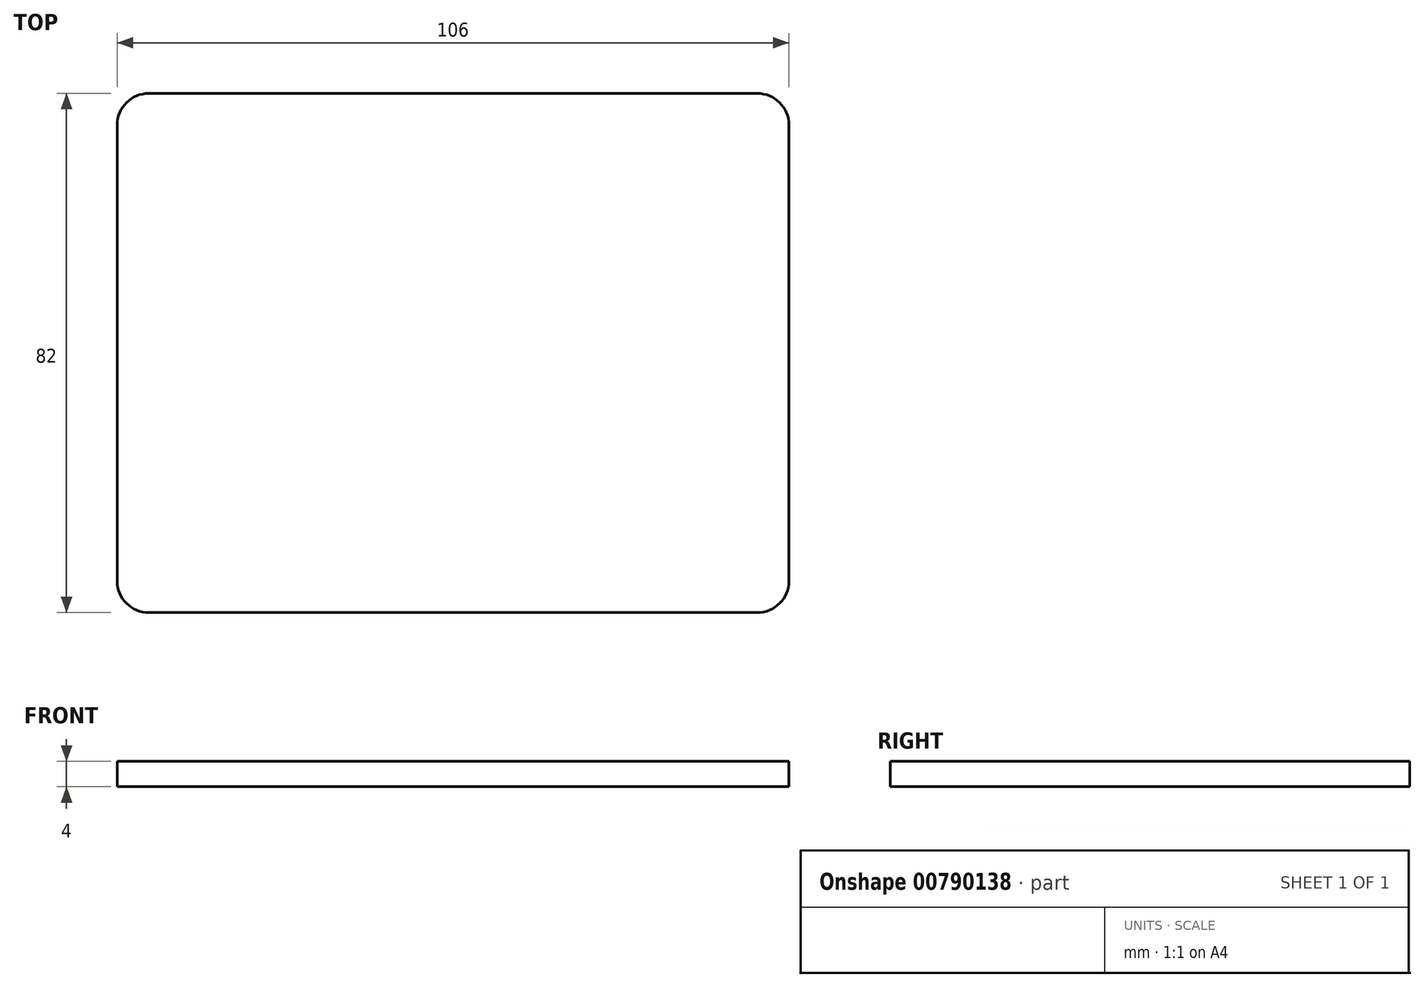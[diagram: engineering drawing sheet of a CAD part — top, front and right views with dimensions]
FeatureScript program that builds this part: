
annotation { "Feature Type Name" : "Feature", "Feature Type Description" : "" }
export const myFeature = defineFeature(function(context is Context, id is Id, definition is map)
    precondition{}
    {
        {
            var Q0;
            Q0=qCreatedBy(makeId("Top.planeOp"),FACE);
            var sketch = newSketch(context, id + "F0", { "sketchPlane" : qUnion([Q0])});
            skLineSegment(sketch, "E0.top", {"start": v(53, -84.5) * mm, "end": v(-53, -84.5) * mm});
            skLineSegment(sketch, "E0.left", {"start": v(53, -2.5) * mm, "end": v(53, -84.5) * mm});
            skLineSegment(sketch, "E0.right", {"start": v(-53, -2.5) * mm, "end": v(-53, -84.5) * mm});
            skPoint(sketch, "E1.orphan", {"position": v(-53, 84.5) * mm});
            skPoint(sketch, "E2.orphan", {"position": v(53, 84.5) * mm});
            skLineSegment(sketch, "E3", {"start": v(-53, -2.5) * mm, "end": v(53, -2.5) * mm});
            skPoint(sketch, "E4.orphan", {"position": v(-53, 7.5) * mm});
            skPoint(sketch, "E5.end.orphan", {"position": v(15.62, 57.1) * mm});
            skPoint(sketch, "E6.orphan", {"position": v(24, 46) * mm});
            skPoint(sketch, "E7.start.orphan", {"position": v(-24, 46) * mm});
            skPoint(sketch, "E8.start.orphan", {"position": v(-18.78, 34.9) * mm});
            skPoint(sketch, "E9.orphan", {"position": v(-45, -2.5) * mm});
            skPoint(sketch, "E10.orphan", {"position": v(45, -2.5) * mm});
            skPoint(sketch, "E11.start.orphan", {"position": v(-18.78, 77.6) * mm});
            skPoint(sketch, "E12.orphan", {"position": v(24, 57.1) * mm});
            skPoint(sketch, "E13", {"position": v(0, 101.9) * mm});
            skPoint(sketch, "E14.end.orphan", {"position": v(50.45, 84.5) * mm});
            skPoint(sketch, "E15.trimOffspring.start.orphan", {"position": v(26.9, 84.5) * mm});
            skPoint(sketch, "E16.end.orphan", {"position": v(0.05, 10.43) * mm});
            skPoint(sketch, "E16.start.orphan", {"position": v(-23.5, 12.91) * mm});
            skPoint(sketch, "E17.orphan", {"position": v(23.5, 57.1) * mm});
            skPoint(sketch, "E18.orphan", {"position": v(24, 7.5) * mm});
            skPoint(sketch, "E19.orphan", {"position": v(-24, 7.5) * mm});
            skPoint(sketch, "E20.end.orphan", {"position": v(-23.5, 32.3) * mm});
            skPoint(sketch, "E20.start.orphan", {"position": v(-23.5, 14.75) * mm});
            skPoint(sketch, "E21.start.orphan", {"position": v(-23.5, 34.8) * mm});
            skPoint(sketch, "E22.right.start.orphan", {"position": v(24, 84.5) * mm});
            skPoint(sketch, "E23.end.orphan", {"position": v(23.5, 59.6) * mm});
            skPoint(sketch, "E23.start.orphan", {"position": v(23.5, 77.5) * mm});
            skPoint(sketch, "E22.bottom.start.orphan", {"position": v(-24, 84.5) * mm});
            skPoint(sketch, "E24.orphan", {"position": v(5, 7.5) * mm});
            skPoint(sketch, "E25.orphan", {"position": v(-5, 7.5) * mm});
            skSolve(sketch);
        }
        {
            var Q0;
            Q0=makeQuery(id+"F0.imprint","IMPRINT",FACE,{"disambiguationData":[TD([[makeQuery(id+"F0.imprint","IMPRINT",EDGE,{"derivedFrom":sQuery(id+"F0.wireOp",EDGE,"E0.top")}),-1.0]])]});
            var Q1;
            Q1=makeQuery(id+"FFKYT1JyJelcZBP_0.imprint","IMPRINT",FACE,{"disambiguationData":[TD([[makeQuery(id+"FFKYT1JyJelcZBP_0.imprint","IMPRINT",EDGE,{"derivedFrom":sQuery(id+"FFKYT1JyJelcZBP_0.wireOp",EDGE,"c95b5e24-0e9f-48d9-b100-8ac08296f345.bottom")}),1.0]])]});
            var Q2;
            {var subQ5=sQuery(id+"FFKYT1JyJelcZBP_0.wireOp",EDGE,"56e8594c-ecf8-4cb0-9939-2472721651db");Q2=makeQuery(id+"FFKYT1JyJelcZBP_0.imprint","IMPRINT",FACE,{"disambiguationData":[TD([[makeQuery(id+"FFKYT1JyJelcZBP_0.imprint","IMPRINT",EDGE,{"derivedFrom":subQ5}),-1.0]])]});}
            var Q3;
            Q3=makeQuery(id+"FFKYT1JyJelcZBP_0.imprint","IMPRINT",FACE,{"disambiguationData":[TD([[makeQuery(id+"FFKYT1JyJelcZBP_0.imprint","IMPRINT",EDGE,{"derivedFrom":sQuery(id+"FFKYT1JyJelcZBP_0.wireOp",EDGE,"2df63ac5-1c92-4d20-afe2-e4802780a0be.top")}),1.0]])]});
            var Q4;
            Q4=makeQuery(id+"F0.imprint","IMPRINT",FACE,{"disambiguationData":[TD([[makeQuery(id+"F0.imprint","IMPRINT",EDGE,{"derivedFrom":sQuery(id+"F0.wireOp",EDGE,"waGpoIm7-0Mzt-1UnA-IRLj-dOBubJTwNrkn.bottom")}),-1.0]])]});
            var Q5;
            Q5=makeQuery(id+"FFKYT1JyJelcZBP_0.imprint","IMPRINT",FACE,{"disambiguationData":[TD([[makeQuery(id+"FFKYT1JyJelcZBP_0.imprint","IMPRINT",EDGE,{"derivedFrom":sQuery(id+"FFKYT1JyJelcZBP_0.wireOp",EDGE,"5a77a93a-04a2-4624-8db7-a53228818b46")}),1.0]])]});
            var Q6;
            Q6=makeQuery(id+"FFKYT1JyJelcZBP_0.imprint","IMPRINT",FACE,{"disambiguationData":[TD([[makeQuery(id+"FFKYT1JyJelcZBP_0.imprint","IMPRINT",EDGE,{"derivedFrom":sQuery(id+"FFKYT1JyJelcZBP_0.wireOp",EDGE,"64439ff4-f162-4608-b04a-86becdaf6998")}),1.0]])]});
            extrude(context, id + "F1", {"entities" : qUnion([Q0, Q1, Q2, Q3, Q4, Q5, Q6]), "depth" : 4 * mm});
        }
        {
            var Q0;
            Q0=makeQuery(id+"F1.opExtrude","SWEPT_EDGE",EDGE,{"disambiguationData":[OSD([sQuery(id+"F0.wireOp",EDGE,"E0.top"),sQuery(id+"F0.wireOp",EDGE,"E0.left")])]});
            var Q1;
            Q1=makeQuery(id+"F1.opExtrude","SWEPT_EDGE",EDGE,{"disambiguationData":[OSD([sQuery(id+"F0.wireOp",EDGE,"E0.top"),sQuery(id+"F0.wireOp",EDGE,"E0.right")])]});
            var Q2;
            Q2=makeQuery(id+"F1.opExtrude","SWEPT_EDGE",EDGE,{"disambiguationData":[OSD([sQuery(id+"F0.wireOp",EDGE,"E0.right"),sQuery(id+"F0.wireOp",EDGE,"E3")])]});
            var Q3;
            Q3=makeQuery(id+"F1.opExtrude","SWEPT_EDGE",EDGE,{"disambiguationData":[OSD([sQuery(id+"F0.wireOp",EDGE,"E0.left"),sQuery(id+"F0.wireOp",EDGE,"E3")])]});
            var Q4;
            Q4=makeQuery(id+"F1.opExtrude","SWEPT_EDGE",EDGE,{"disambiguationData":[OSD([sQuery(id+"FFKYT1JyJelcZBP_0.wireOp",EDGE,"fc6cac5f-266f-4da8-866d-79a4c6e8a072.top"),sQuery(id+"FFKYT1JyJelcZBP_0.wireOp",EDGE,"fc6cac5f-266f-4da8-866d-79a4c6e8a072.left")])]});
            var Q5;
            Q5=makeQuery(id+"F1.opExtrude","SWEPT_EDGE",EDGE,{"disambiguationData":[OSD([sQuery(id+"FFKYT1JyJelcZBP_0.wireOp",EDGE,"fc6cac5f-266f-4da8-866d-79a4c6e8a072.top"),sQuery(id+"FFKYT1JyJelcZBP_0.wireOp",EDGE,"fc6cac5f-266f-4da8-866d-79a4c6e8a072.right")])]});
            fillet(context, id + "F2", {"entities" : qUnion([Q0, Q1, Q2, Q3, Q4, Q5]), "radius" : 5 * mm, "tangentPropagation" : true, "allowEdgeOverflow" : false});
        }
    });
